# Revit family: LAMP_FIL 45 2240MM OPAL SUSPENDED
name_source: partatom
category: Luminarias
revit_build: Autodesk Revit 2018 (Build: 20170223_1515(x64)
units: mm (PartAtom-declared; Revit-internal decimal feet)

## family parameters
Anfitrión = Cara
Compartido = No
Corte con vacíos al cargar = No
Cota de conector redondo = Diámetro de uso
Origen de luz = Sí
Punto de cálculo de habitación = No
Tipo de pieza = Normal

## types (24) — shared parameters
CRI = 80
Cambio de temperatura de color de luz atenuada = <Ninguno>
Dimensions = 2240x45x80
Elevación por defecto = 1219 mm
Fabricante = LAMP
Filtro de color = 16777215
Gear = Electronic
IEE = A+
Installation instructions = https://www.lamp.es
Insulation class = I
Lamp = MID-POWER LED
Last update = 17/03/2021
Longitud de línea de emisión = 2240 mm  [stored 7.34908 ft]
MacAdam = 3
Manufacturer URL = http://www.lamp.es
Manufacturer country = Spain
Manufacturer name = LAMP
Material difusor = LAMP_PC Difusor Opal Fil
Material suspension = LAMP_Acero genérico
Power Supply = 220-240V 50/60Hz
Product URL = https://www.lamp.es
Product datasheet = http://www.lamp.es
Protection rating = IP20 / IK07
Type = MID POWER TRIDONIC
Ángulo de inclinación = -90.00°

## per-type parameters (varying)
| type | Archivo de red fotométrica | Descripción | Efficacy | Finish | LED Lifetime | Material perfil | Modelo | Plum | Power | Product code | Weight |
| 5200LM 3000K DALI BLACK | F41SF224MOOP830nB.IES | FIL45 SUR 2240 5200 WW OPAL DALI BK. | 93 lm/W | Matte black RAL 9011 | 70.000 L80 B10 | LAMP_Aluminio Perfil Fil NG | F41SF224MOOP830DB | 37 W | 31 W | F41SF224MOOP830DB | 5.09 kg |
| 5200LM 3000K DALI GREY | F41SF224MOOP830nG.IES | FIL45 SUR 2240 5200 WW OPAL DALI GR. | 93 lm/W | Gloss grey | 70.000 L80 B10 | LAMP_Aluminio Perfil Fil GR | F41SF224MOOP830DG | 37 W | 31 W | F41SF224MOOP830DG | 5.09 kg |
| 5200LM 3000K DALI WHITE | F41SF224MOOP830nW.IES | FIL45 SUR 2240 5200 WW OPAL DALI WH. | 93 lm/W | Matte white RAL 9010 | 70.000 L80 B10 | LAMP_Aluminio Perfil Fil BL | F41SF224MOOP830DW | 37 W | 31 W | F41SF224MOOP830DW | 5.09 kg |
| 5200LM 3000K  BLACK | F41SF224MOOP830NB.IES | FIL45 SUR 2240 5200 WW OPAL BK. | 93 lm/W | Matte black RAL 9011 | 70.000 L80 B10 | LAMP_Aluminio Perfil Fil NG | F41SF224MOOP830NB | 37 W | 31 W | F41SF224MOOP830NB | 4.80 kg |
| 5200LM 3000K  GREY | F41SF224MOOP830NG.IES | FIL45 SUR 2240 5200 WW OPAL GR. | 93 lm/W | Gloss grey | 70.000 L80 B10 | LAMP_Aluminio Perfil Fil GR | F41SF224MOOP830NG | 37 W | 31 W | F41SF224MOOP830NG | 4.80 kg |
| 5200LM 3000K  WHITE | F41SF224MOOP830NW.IES | FIL45 SUR 2240 5200 WW OPAL WH. | 93 lm/W | Matte white RAL 9010 | 70.000 L80 B10 | LAMP_Aluminio Perfil Fil BL | F41SF224MOOP830NW | 37 W | 31 W | F41SF224MOOP830NW | 4.80 kg |
| 5200LM 4000K DALI BLACK | F41SF224MOOP840nB.IES | FIL45 SUR 2240 5200 NW OPAL DALI BK. | 98 lm/W | Matte black RAL 9011 | 70.000 L80 B10 | LAMP_Aluminio Perfil Fil NG | F41SF224MOOP840DB | 37 W | 31 W | F41SF224MOOP840DB | 5.09 kg |
| 5200LM 4000K DALI GREY | F41SF224MOOP840nG.IES | FIL45 SUR 2240 5200 NW OPAL DALI GR. | 98 lm/W | Gloss grey | 70.000 L80 B10 | LAMP_Aluminio Perfil Fil GR | F41SF224MOOP840DG | 37 W | 31 W | F41SF224MOOP840DG | 5.09 kg |
| 5200LM 4000K DALI WHITE | F41SF224MOOP840nW.IES | FIL45 SUR 2240 5200 NW OPAL DALI WH. | 98 lm/W | Matte white RAL 9010 | 70.000 L80 B10 | LAMP_Aluminio Perfil Fil BL | F41SF224MOOP840DW | 37 W | 31 W | F41SF224MOOP840DW | 5.09 kg |
| 5200LM 4000K  BLACK | F41SF224MOOP840NB.IES | FIL45 SUR 2240 5200 NW OPAL BK. | 98 lm/W | Matte black RAL 9011 | 70.000 L80 B10 | LAMP_Aluminio Perfil Fil NG | F41SF224MOOP840NB | 37 W | 31 W | F41SF224MOOP840NB | 4.80 kg |
| 5200LM 4000K  GREY | F41SF224MOOP840NG.IES | FIL45 SUR 2240 5200 NW OPAL GR. | 98 lm/W | Gloss grey | 70.000 L80 B10 | LAMP_Aluminio Perfil Fil GR | F41SF224MOOP840NG | 37 W | 31 W | F41SF224MOOP840NG | 4.80 kg |
| 5200LM 4000K  WHITE | F41SF224MOOP840NW.IES | FIL45 SUR 2240 5200 NW OPAL WH. | 98 lm/W | Matte white RAL 9010 | 70.000 L80 B10 | LAMP_Aluminio Perfil Fil BL | F41SF224MOOP840NW | 37 W | 31 W | F41SF224MOOP840NW | 4.80 kg |
| 12400LM 3000K DALI BLACK | F41SF224HOOP830nB.IES | FIL45 SUR 2240 12400 WW OPAL DALI BK. | 93 lm/W | Matte black RAL 9011 | 72.000 L80 B10 | LAMP_Aluminio Perfil Fil NG | F41SF224HOOP830DB | 81 W | 72 W | F41SF224HOOP830DB | 5.12 kg |
| 12400LM 3000K DALI GREY | F41SF224HOOP830nG.IES | FIL45 SUR 2240 12400 WW OPAL DALI GR. | 93 lm/W | Gloss grey | 72.000 L80 B10 | LAMP_Aluminio Perfil Fil GR | F41SF224HOOP830DG | 81 W | 72 W | F41SF224HOOP830DG | 5.12 kg |
| 12400LM 3000K DALI WHITE | F41SF196MOOP830NB.IES | FIL45 SUR 2240 12400 WW OPAL DALI WH. | 93 lm/W | Matte white RAL 9010 | 72.000 L80 B10 | LAMP_Aluminio Perfil Fil BL | F41SF224HOOP830DW | 81 W | 72 W | F41SF224HOOP830DW | 5.12 kg |
| 12400LM 3000K  BLACK | F41SF224HOOP830NB.IES | FIL45 SUR 2240 12400 WW OPAL BK. | 93 lm/W | Matte black RAL 9011 | 72.000 L80 B10 | LAMP_Aluminio Perfil Fil NG | F41SF224HOOP830NB | 81 W | 72 W | F41SF224HOOP830NB | 4.90 kg |
| 12400LM 3000K  GREY | F41SF224HOOP830NG.IES | FIL45 SUR 2240 12400 WW OPAL GR. | 93 lm/W | Gloss grey | 72.000 L80 B10 | LAMP_Aluminio Perfil Fil GR | F41SF224HOOP830NG | 81 W | 72 W | F41SF224HOOP830NG | 4.90 kg |
| 12400LM 3000K  WHITE | F41SF224HOOP830NW.IES | FIL45 SUR 2240 12400 WW OPAL WH. | 93 lm/W | Matte white RAL 9010 | 72.000 L80 B10 | LAMP_Aluminio Perfil Fil BL | F41SF224HOOP830NW | 81 W | 72 W | F41SF224HOOP830NW | 4.90 kg |
| 12400LM 4000K DALI BLACK | F41SF224HOOP840nB.IES | 45 SUR 2240 12400 NW OPAL DALI BK. | 93 lm/W | Matte black RAL 9011 | 72.000 L80 B10 | LAMP_Aluminio Perfil Fil NG | F41SF224HOOP840DB | 81 W | 72 W | F41SF224HOOP840DB | 5.12 kg |
| 12400LM 4000K DALI GREY | F41SF224HOOP840nG.IES | FIL45 SUR 2240 12400 NW OPAL DALI GR. | 93 lm/W | Gloss grey | 72.000 L80 B10 | LAMP_Aluminio Perfil Fil GR | F41SF224HOOP840DG | 81 W | 72 W | F41SF224HOOP840DG | 5.12 kg |
| 12400LM 4000K DALI WHITE | F41SF224HOOP840nW.IES | FIL45 SUR 2240 12400 NW OPAL DALI WH. | 93 lm/W | Matte white RAL 9010 | 72.000 L80 B10 | LAMP_Aluminio Perfil Fil BL | F41SF224HOOP840DW | 81 W | 72 W | F41SF224HOOP840DW | 5.12 kg |
| 12400LM 4000K  BLACK | F41SF224HOOP840NB.IES | FIL45 SUR 2240 12400 NW OPAL BK. | 93 lm/W | Matte black RAL 9011 | 72.000 L80 B10 | LAMP_Aluminio Perfil Fil NG | F41SF224HOOP840NB | 81 W | 72 W | F41SF224HOOP840NB | 4.90 kg |
| 12400LM 4000K  GREY | F41SF224HOOP840NG.IES | FIL45 SUR 2240 12400 NW OPAL GR. | 93 lm/W | Gloss grey | 72.000 L80 B10 | LAMP_Aluminio Perfil Fil GR | F41SF224HOOP840NG | 81 W | 72 W | F41SF224HOOP840NG | 4.90 kg |
| 12400LM 4000K  WHITE | F41SF224HOOP840NW.IES | FIL45 SUR 2240 12400 NW OPAL WH. | 93 lm/W | Matte white RAL 9010 | 72.000 L80 B10 | LAMP_Aluminio Perfil Fil BL | F41SF224HOOP840NW | 81 W | 72 W | F41SF224HOOP840NW | 4.90 kg |

note: [stored X ft] marks values corroborated as IEEE doubles in the binary element streams (Revit-internal decimal feet)
